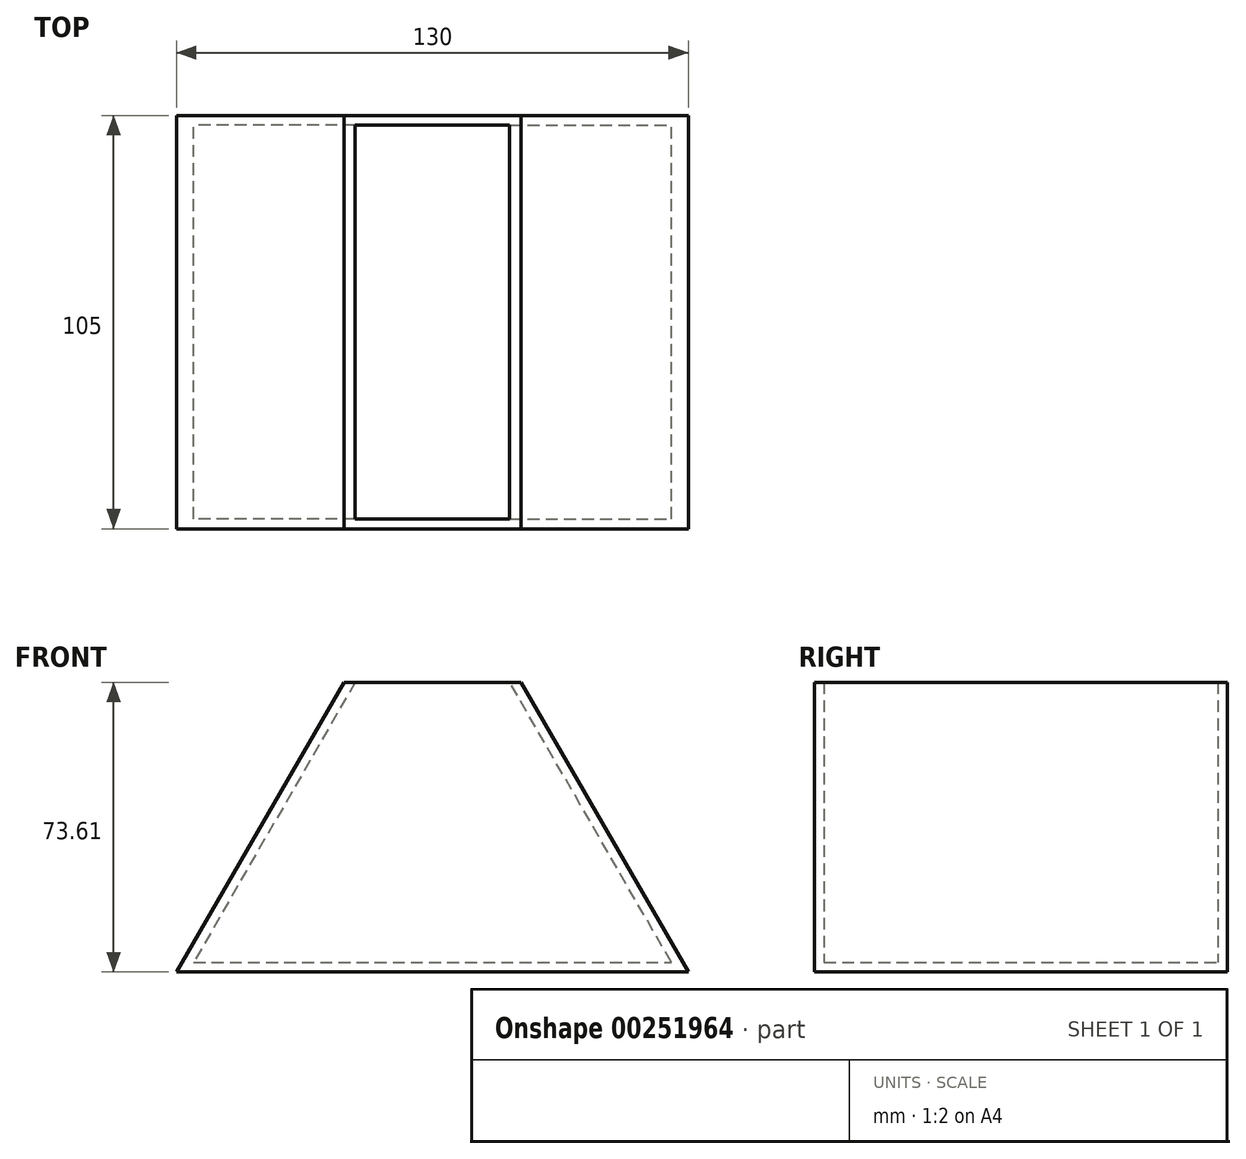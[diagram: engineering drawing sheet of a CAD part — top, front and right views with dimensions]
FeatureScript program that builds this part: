
annotation { "Feature Type Name" : "Feature", "Feature Type Description" : "" }
export const myFeature = defineFeature(function(context is Context, id is Id, definition is map)
    precondition{}
    {
        {
            var Q0;
            Q0=qCreatedBy(makeId("Front.planeOp"),FACE);
            var sketch = newSketch(context, id + "F0", { "sketchPlane" : qUnion([Q0])});
            skLineSegment(sketch, "E0", {"start": v(-90.96, 0) * mm, "end": v(39.04, 0) * mm});
            skLineSegment(sketch, "E1", {"start": v(39.04, 0) * mm, "end": v(-3.46, 73.61) * mm});
            skLineSegment(sketch, "E2", {"start": v(-3.46, 73.61) * mm, "end": v(-48.46, 73.61) * mm});
            skLineSegment(sketch, "E3", {"start": v(-48.46, 73.61) * mm, "end": v(-90.96, 0) * mm});
            skSolve(sketch);
        }
        {
            var Q0;
            Q0 = qSketchRegion(id + "F0", true);
            var Q1;
            Q1=makeQuery(id+"F0.imprint","IMPRINT",FACE,{"disambiguationData":[TD([[makeQuery(id+"F0.imprint","IMPRINT",EDGE,{"derivedFrom":sQuery(id+"F0.wireOp",EDGE,"E0")}),1.0]])]});
            extrude(context, id + "F1", {"entities" : qUnion([Q0, Q1]), "depth" : 105 * mm});
        }
        {
            var Q0;
            Q0=makeQuery(id+"F1.opExtrude","SWEPT_FACE",FACE,{"disambiguationData":[OSD([sQuery(id+"F0.wireOp",EDGE,"E2")])]});
            shell(context, id + "F2", {"entities" : qUnion([Q0]), "thickness" : 2.5 * mm});
        }
    });
